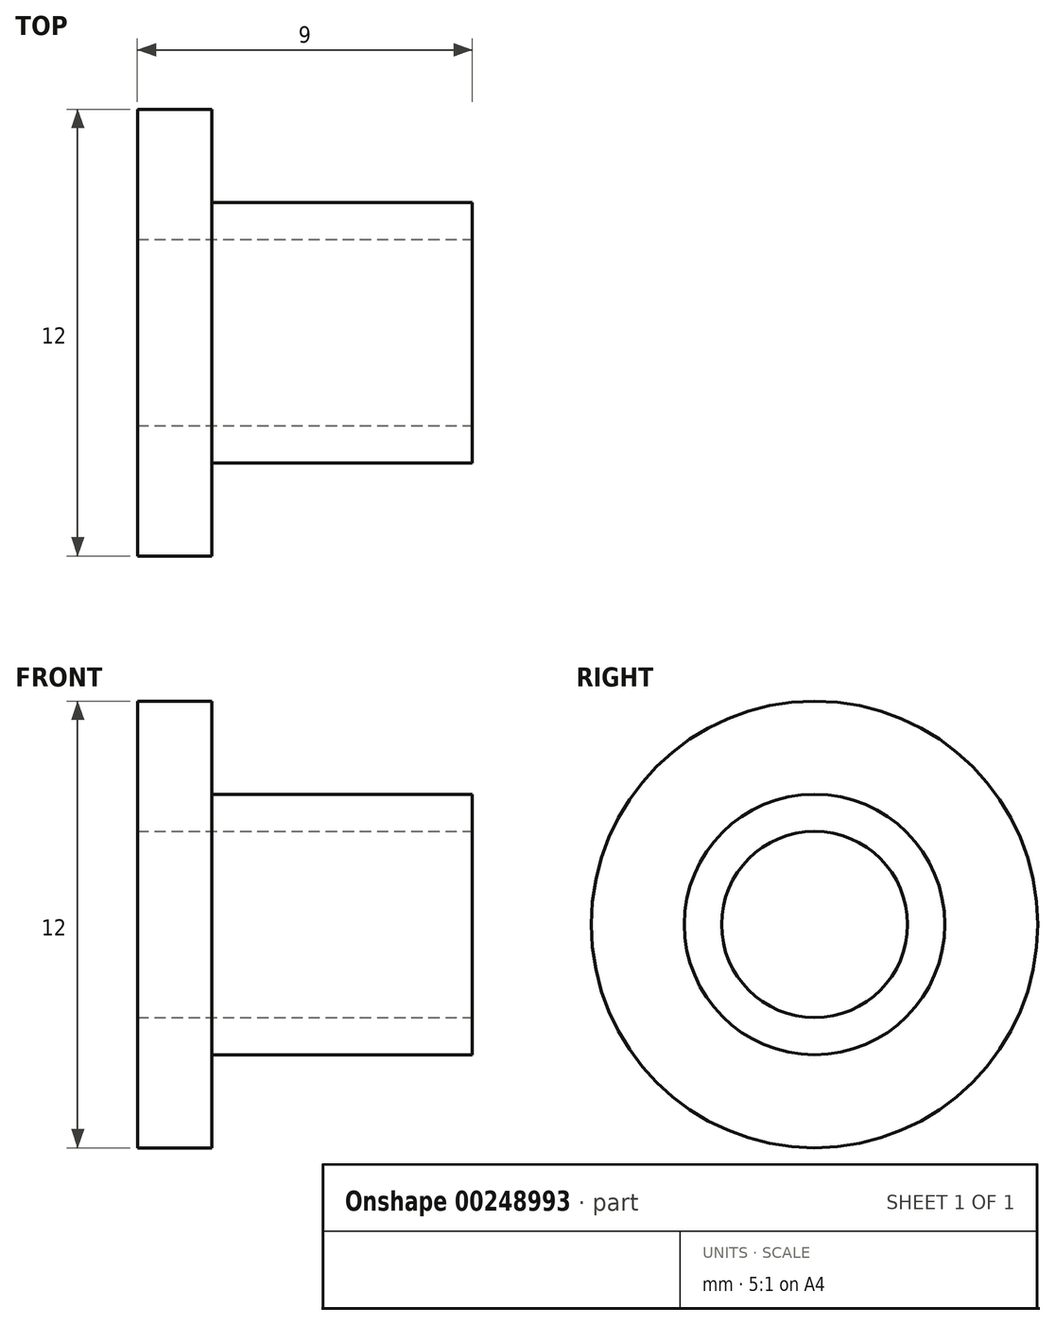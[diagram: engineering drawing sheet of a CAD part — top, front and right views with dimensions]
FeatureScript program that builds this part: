
annotation { "Feature Type Name" : "Feature", "Feature Type Description" : "" }
export const myFeature = defineFeature(function(context is Context, id is Id, definition is map)
    precondition{}
    {
        {
            var Q0;
            Q0=qCreatedBy(makeId("Front.planeOp"),FACE);
            var sketch = newSketch(context, id + "F0", { "sketchPlane" : qUnion([Q0])});
            skLineSegment(sketch, "E0", {"start": v(-5.23, 2.5) * mm, "end": v(-5.23, 6) * mm});
            skLineSegment(sketch, "E1", {"start": v(-5.23, 6) * mm, "end": v(-3.23, 6) * mm});
            skLineSegment(sketch, "E2", {"start": v(-3.23, 6) * mm, "end": v(-3.23, 3.5) * mm});
            skLineSegment(sketch, "E3", {"start": v(-3.23, 3.5) * mm, "end": v(3.77, 3.5) * mm});
            skLineSegment(sketch, "E4", {"start": v(3.77, 3.5) * mm, "end": v(3.77, 2.5) * mm});
            skLineSegment(sketch, "E5", {"start": v(3.77, 0) * mm, "end": v(-5.23, 0) * mm});
            skLineSegment(sketch, "E6", {"start": v(-5.23, 2.5) * mm, "end": v(3.77, 2.5) * mm});
            skSolve(sketch);
        }
        {
            var Q0;
            Q0=makeQuery(id+"F0.imprint","IMPRINT",FACE,{"disambiguationData":[TD([[makeQuery(id+"F0.imprint","IMPRINT",EDGE,{"derivedFrom":sQuery(id+"F0.wireOp",EDGE,"E0")}),-1.0]])]});
            var Q1;
            Q1=sQuery(id+"F0.wireOp",EDGE,"E5");
            revolve(context, id + "F1", {"entities" : qUnion([Q0]), "axis" : qUnion([Q1]), "revolveType" : RevolveType.FULL});
        }
    });
